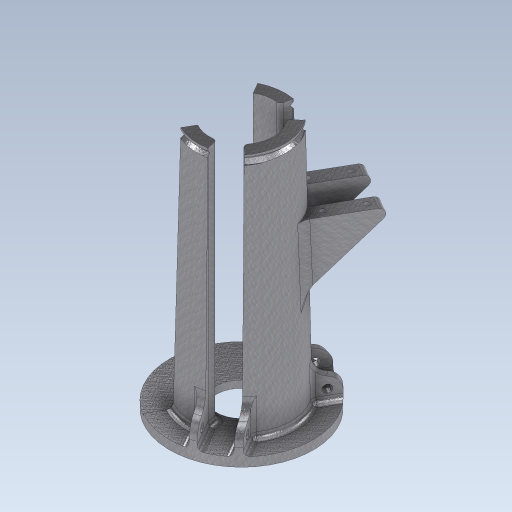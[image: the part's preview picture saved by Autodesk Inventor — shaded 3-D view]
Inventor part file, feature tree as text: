
AUTODESK INVENTOR PART (.ipt)
format: ipt  version: 2023 (Build 270158000, 158)  size: 796,672 bytes
history: native  units: in
note: dims shown in document units (in); Inventor stores cm internally (conversion verified against a paired STEP export)
features: projected_geometry x8, sketch x7, extrude x5, revolve x5, fillet x3, hole x2, direct_edit x2, pattern_circular x1, plane x1
ambient origin geometry x8: Origin, YZ Plane, XZ Plane, XY Plane, X Axis, Y Axis, Z Axis, Center Point
bodies: Solid1 (feature_tree)
feature tree (34):
  sketch  "Sketch2"  dims[d0=1.0in d1=1.4038in]
  extrude  "Extrusion1"  Depth=1.4038in
  extrude  "Extrusion2"  TaperAngle=120.0deg  [1 undecoded]
  extrude  "Extrusion3"  Depth=0.481in
  hole  "Hole1"  [1 undecoded]
  pattern_circular  "Circular Pattern1"  Count=14  [1 undecoded]
  sketch  "Sketch5"  dims[d6=0.8987in d7=0.7874in d9=120.0deg]
  fillet  "Fillet1"  Radius=0.1378in
  extrude  "Extrusion5"  Depth=0.1378in
  plane  "Work Plane1"
  direct_edit  "Direct Edit3"
  extrude  "Extrusion6"  Depth=0.5906in
  hole  "Hole2"  [1 undecoded]
  direct_edit  "Direct Edit2"
  fillet  "Fillet2"  Radius=0.7874in
  fillet  "Fillet3"  Radius=0.1181in
  revolve  "Revolution1"  [1 undecoded]
  sketch  "Sketch3"  dims[d2=3.1496in d3=120.0deg]
  projected_geometry  "Projected Loop1"
  projected_geometry  "Projected Loop2"
  projected_geometry  "Projected Loop3"
  projected_geometry  "Projected Loop4"
  sketch  "Sketch4"  dims[d4=0.5906in d5=0.481in]
  projected_geometry  "Projected Loop5"
  sketch  "Sketch7"  dims[d11=0.8987in]
  sketch  "Sketch8"  dims[d13=120.0deg]
  projected_geometry  "Projected Loop6"
  projected_geometry  "Projected Loop7"
  sketch  "Sketch10"  dims[d14=0.1969in d15=0.0in d17=5.5118in d18=0.0in d19=0.1378in d20=0.1378in d21=0.5906in d22=0.4961in d23=0.0in d24=0.7874in d25=120.0deg d27=0.1181in d28=0.1772in d29=0.2362in d30=0.1575in d31=0.0787in d32=90.0deg d33=0.315in d34=0.8108in d35=0.3937in d39=1.0945in d40=0.0787in d41=0.0394in d42=0.0in d43=0.1181in d44=0.315in d45=-1.6614in d46=0.3228in d47=1.2795in d48=0.7087in d49=1.2644in d50=0.1173in d51=1.378in d52=0.0in d54=-0.323in d55=0.2362in d56=0.2362in d57=0.1575in d58=0.0787in d59=90.0deg d60=1.2598in d61=0.8108in d63=0.0103in d64=-0.0103in d65=-0.0103in d66=0.1181in d67=0.0787in d68=360.0deg d69=0.0344in]
  projected_geometry  "Projected Loop8"
  revolve  "Rotate2"  [1 undecoded]
  revolve  "Rotate3"  [1 undecoded]
  revolve  "Rotate4"  [1 undecoded]
  revolve  "Rotate5"  [1 undecoded]
note: 9 required parameter values undecoded (feature->parameter linkage not recoverable at this tier; creation-order binding heuristic only, values carry confidence <= 0.55)